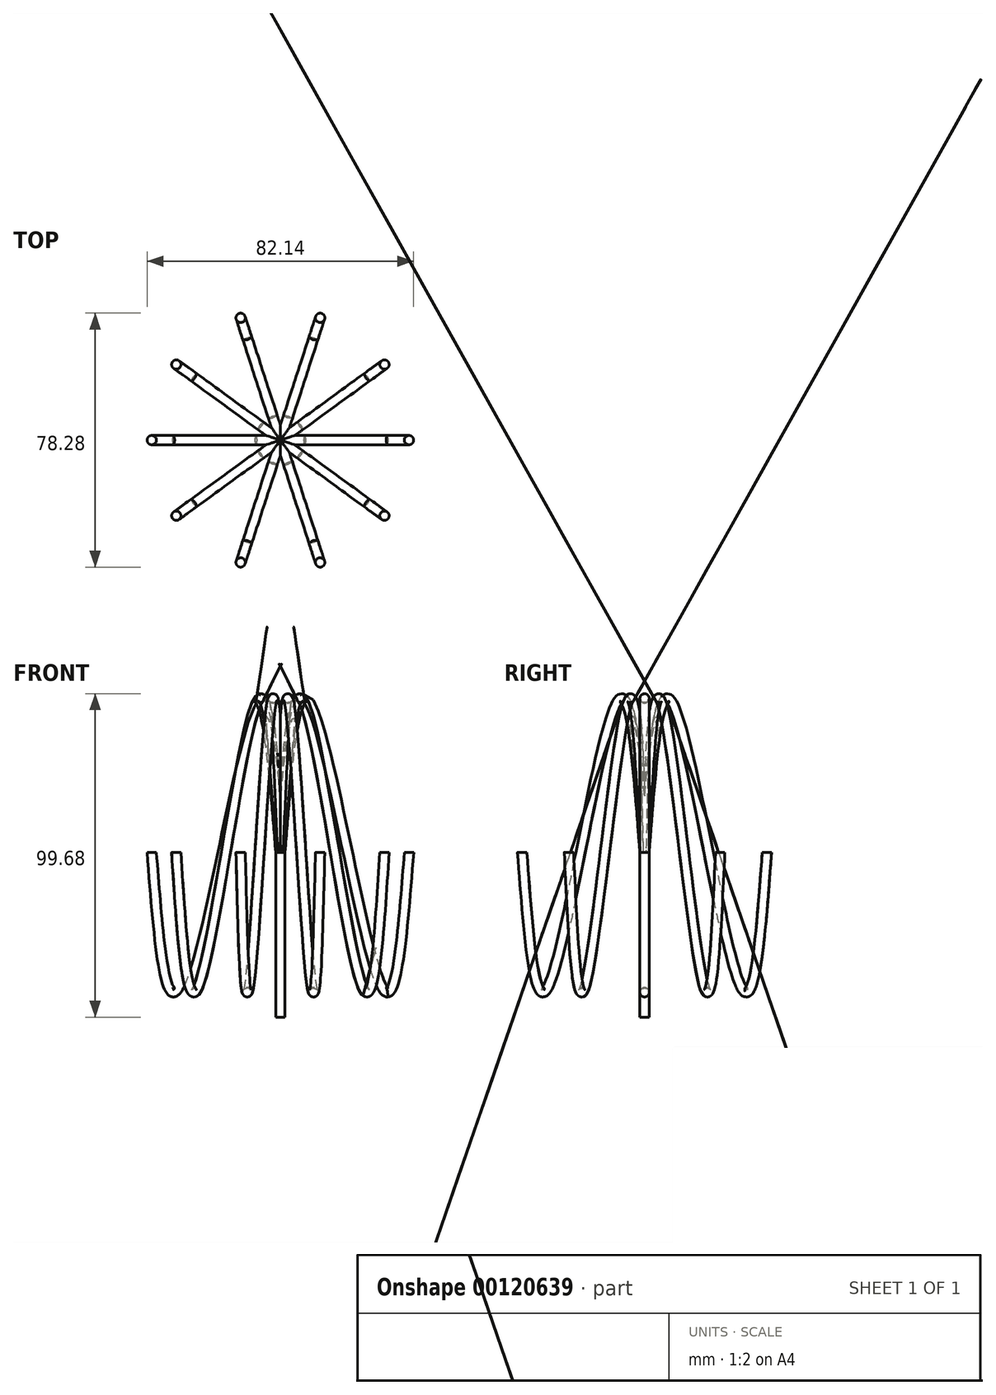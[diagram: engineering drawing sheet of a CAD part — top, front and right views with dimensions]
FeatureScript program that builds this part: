
annotation { "Feature Type Name" : "Feature", "Feature Type Description" : "" }
export const myFeature = defineFeature(function(context is Context, id is Id, definition is map)
    precondition{}
    {
        {
            var Q0;
            Q0=qCreatedBy(makeId("Front.planeOp"),FACE);
            var sketch = newSketch(context, id + "F0", { "sketchPlane" : qUnion([Q0])});
            skFitSpline(sketch, "E0", {"points": [v(0, 0) * mm, v(8.69, 46.52) * mm, v(31.8, -42.28) * mm, v(39.63, 0) * mm], "startDerivative": vector(21.13, 264.63) * mm, "endDerivative": vector(19.59, 252.75) * mm});
            skSolve(sketch);
        }
        {
            var Q0;
            Q0=qCreatedBy(makeId("Top.planeOp"),FACE);
            var sketch = newSketch(context, id + "F1", { "sketchPlane" : qUnion([Q0])});
            skCircle(sketch, "E1", {"center": v(0, 0) * mm, "radius": 1.44 * mm});
            skSolve(sketch);
        }
        {
            var Q0;
            Q0=makeQuery(id+"F1.imprint","IMPRINT",FACE,{"disambiguationData":[TD([[makeQuery(id+"F1.imprint","IMPRINT",EDGE,{"derivedFrom":sQuery(id+"F1.wireOp",EDGE,"E1")}),1.0]])]});
            var Q1;
            Q1=sQuery(id+"F0.wireOp",EDGE,"E0");
            sweep(context, id + "F2", {"profiles" : qUnion([Q0]), "path" : qUnion([Q1])});
        }
        {
            var Q0;
            Q0=makeQuery(id+"F2.opSweep","SWEPT_BODY",BODY,{"disambiguationData":[OSD([sQuery(id+"F0.wireOp",EDGE,"E0"),sQuery(id+"F1.wireOp",EDGE,"E1")])]});
            var Q1;
            Q1=makeQuery(id+"F2.opSweep","CAP_EDGE",EDGE,{"disambiguationData":[OSD([sQuery(id+"F0.wireOp",VERTEX,"E0.start"),sQuery(id+"F1.wireOp",EDGE,"E1")])],"isStart":true});
            circularPattern(context, id + "F3", {"operationType" : NewBodyOperationType.ADD, "entities" : qUnion([Q0]), "axis" : qUnion([Q1]), "angle" : 360 * degree, "instanceCount" : 10, "equalSpace" : true});
        }
        {
            var Q0;
            Q0=makeQuery(id+"F2.opSweep","CAP_FACE",FACE,{"disambiguationData":[OSD([sQuery(id+"F0.wireOp",VERTEX,"E0.start"),sQuery(id+"F1.wireOp",EDGE,"E1")])],"isStart":true});
            extrude(context, id + "F4", {"entities" : qUnion([Q0]), "operationType" : NewBodyOperationType.ADD, "depth" : 50.8 * mm});
        }
    });
